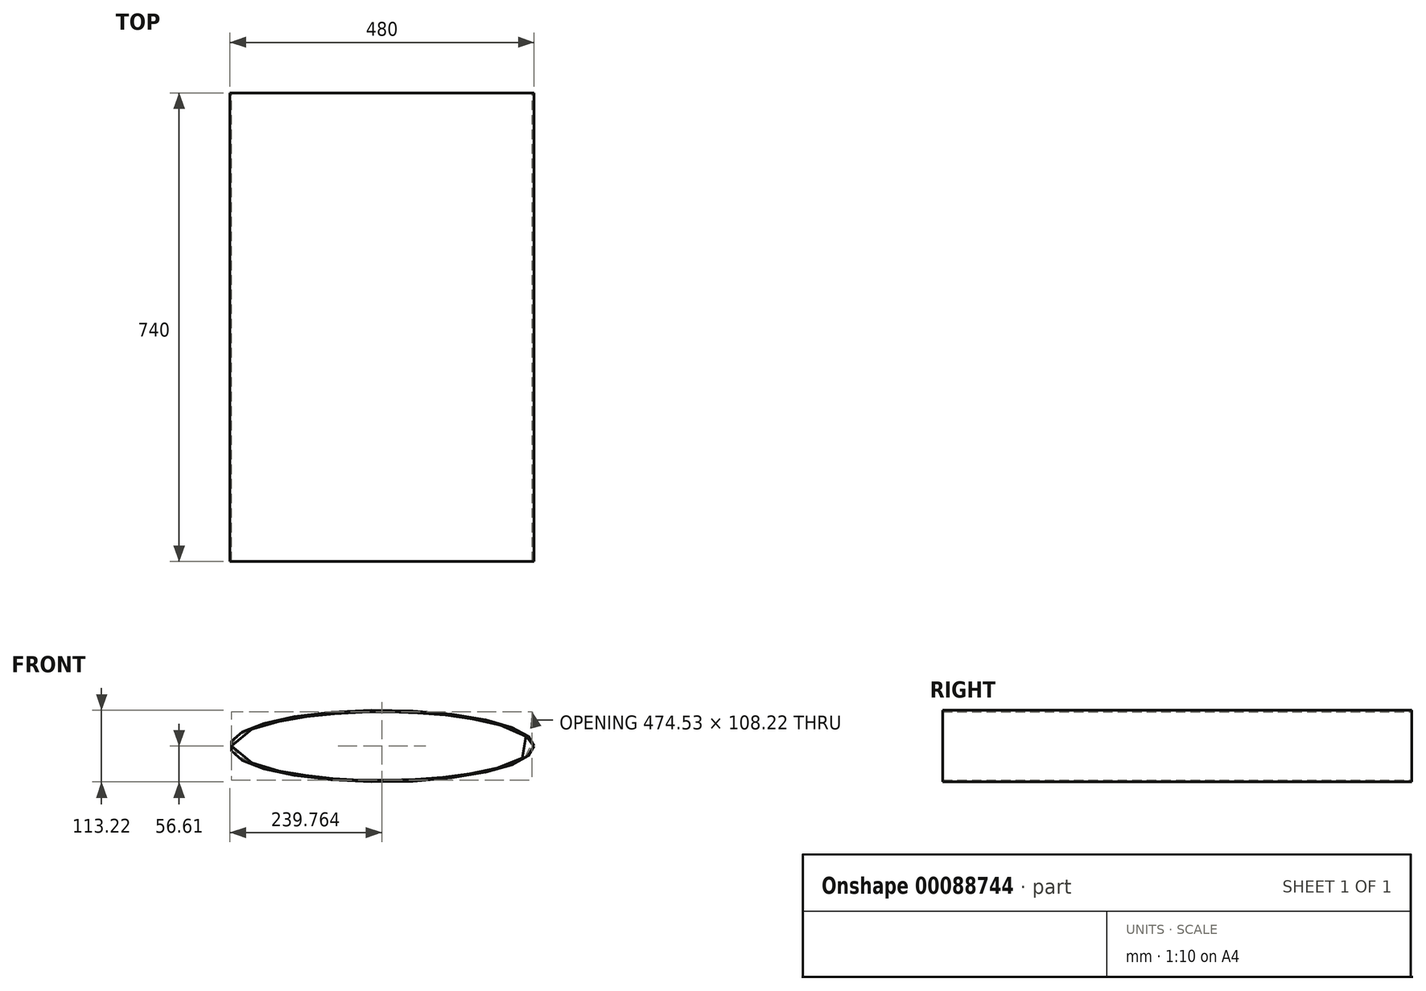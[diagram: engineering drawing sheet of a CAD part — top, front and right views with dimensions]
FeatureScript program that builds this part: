
annotation { "Feature Type Name" : "Feature", "Feature Type Description" : "" }
export const myFeature = defineFeature(function(context is Context, id is Id, definition is map)
    precondition{}
    {
        {
            var Q0;
            Q0=qCreatedBy(makeId("Front.planeOp"),FACE);
            var sketch = newSketch(context, id + "F0", { "sketchPlane" : qUnion([Q0])});
            skEllipse(sketch, "E0", {"center": v(0, 0) * mm, "majorRadius": 240 * mm, "minorRadius": 56.61 * mm, "majorAxis": v(1, 0)});
            skSolve(sketch);
        }
        {
            var Q0;
            Q0 = qSketchRegion(id + "F0", true);
            extrude(context, id + "F1", {"entities" : qUnion([Q0]), "depth" : 740 * mm});
        }
        {
            var Q0;
            Q0=makeQuery(id+"F1.opExtrude","CAP_FACE",FACE,{"disambiguationData":[OSD([sQuery(id+"F0.wireOp",EDGE,"E0")])],"isStart":false});
            var Q1;
            Q1=makeQuery(id+"F1.opExtrude","CAP_FACE",FACE,{"disambiguationData":[OSD([sQuery(id+"F0.wireOp",EDGE,"E0")])],"isStart":true});
            shell(context, id + "F2", {"entities" : qUnion([Q0, Q1]), "thickness" : 2.5 * mm});
        }
    });
